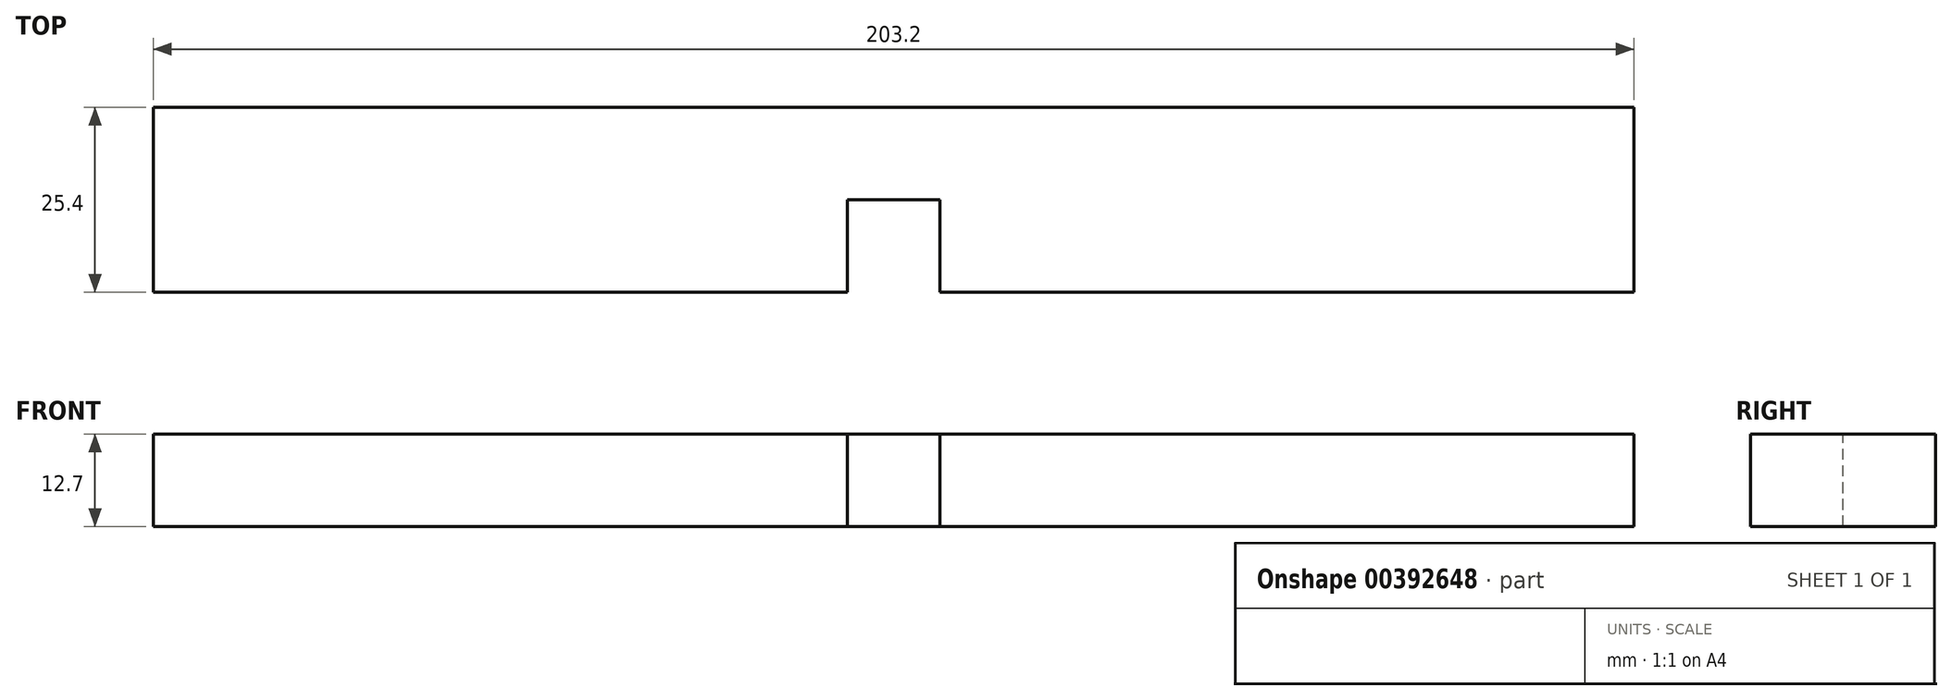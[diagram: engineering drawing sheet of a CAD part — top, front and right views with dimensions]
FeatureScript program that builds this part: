
annotation { "Feature Type Name" : "Feature", "Feature Type Description" : "" }
export const myFeature = defineFeature(function(context is Context, id is Id, definition is map)
    precondition{}
    {
        {
            var Q0;
            Q0=qCreatedBy(makeId("Top.planeOp"),FACE);
            var sketch = newSketch(context, id + "F0", { "sketchPlane" : qUnion([Q0])});
            skLineSegment(sketch, "E0.bottom", {"start": v(-101.6, 12.7) * mm, "end": v(101.6, 12.7) * mm});
            skLineSegment(sketch, "E0.top", {"start": v(-101.6, -12.7) * mm, "end": v(101.6, -12.7) * mm});
            skLineSegment(sketch, "E0.left", {"start": v(-101.6, 12.7) * mm, "end": v(-101.6, -12.7) * mm});
            skLineSegment(sketch, "E0.right", {"start": v(101.6, 12.7) * mm, "end": v(101.6, -12.7) * mm});
            skPoint(sketch, "E0.middle", {"position": v(0, 0) * mm});
            skSolve(sketch);
        }
        {
            var Q0;
            Q0 = qSketchRegion(id + "F0", true);
            extrude(context, id + "F1", {"entities" : qUnion([Q0]), "endBound" : BoundingType.SYMMETRIC, "depth" : 12.7 * mm});
        }
        {
            var Q0;
            Q0=makeQuery(id+"F1.opExtrude","CAP_FACE",FACE,{"disambiguationData":[OSD([sQuery(id+"F0.wireOp",EDGE,"E0.bottom"),sQuery(id+"F0.wireOp",EDGE,"E0.top"),sQuery(id+"F0.wireOp",EDGE,"E0.left"),sQuery(id+"F0.wireOp",EDGE,"E0.right")])],"isStart":false});
            var sketch = newSketch(context, id + "F2", { "sketchPlane" : qUnion([Q0])});
            skLineSegment(sketch, "E1.bottom", {"start": v(-6.35, 0) * mm, "end": v(6.35, 0) * mm});
            skLineSegment(sketch, "E1.top", {"start": v(-6.35, -25.4) * mm, "end": v(6.35, -25.4) * mm});
            skLineSegment(sketch, "E1.left", {"start": v(-6.35, 0) * mm, "end": v(-6.35, -25.4) * mm});
            skLineSegment(sketch, "E1.right", {"start": v(6.35, 0) * mm, "end": v(6.35, -25.4) * mm});
            skPoint(sketch, "E1.middle", {"position": v(0, -12.7) * mm});
            skSolve(sketch);
        }
        {
            var Q0;
            Q0 = qSketchRegion(id + "F2", true);
            extrude(context, id + "F3", {"entities" : qUnion([Q0]), "operationType" : NewBodyOperationType.REMOVE, "endBound" : BoundingType.THROUGH_ALL, "oppositeDirection" : true, "depth" : 25.4 * mm});
        }
    });
